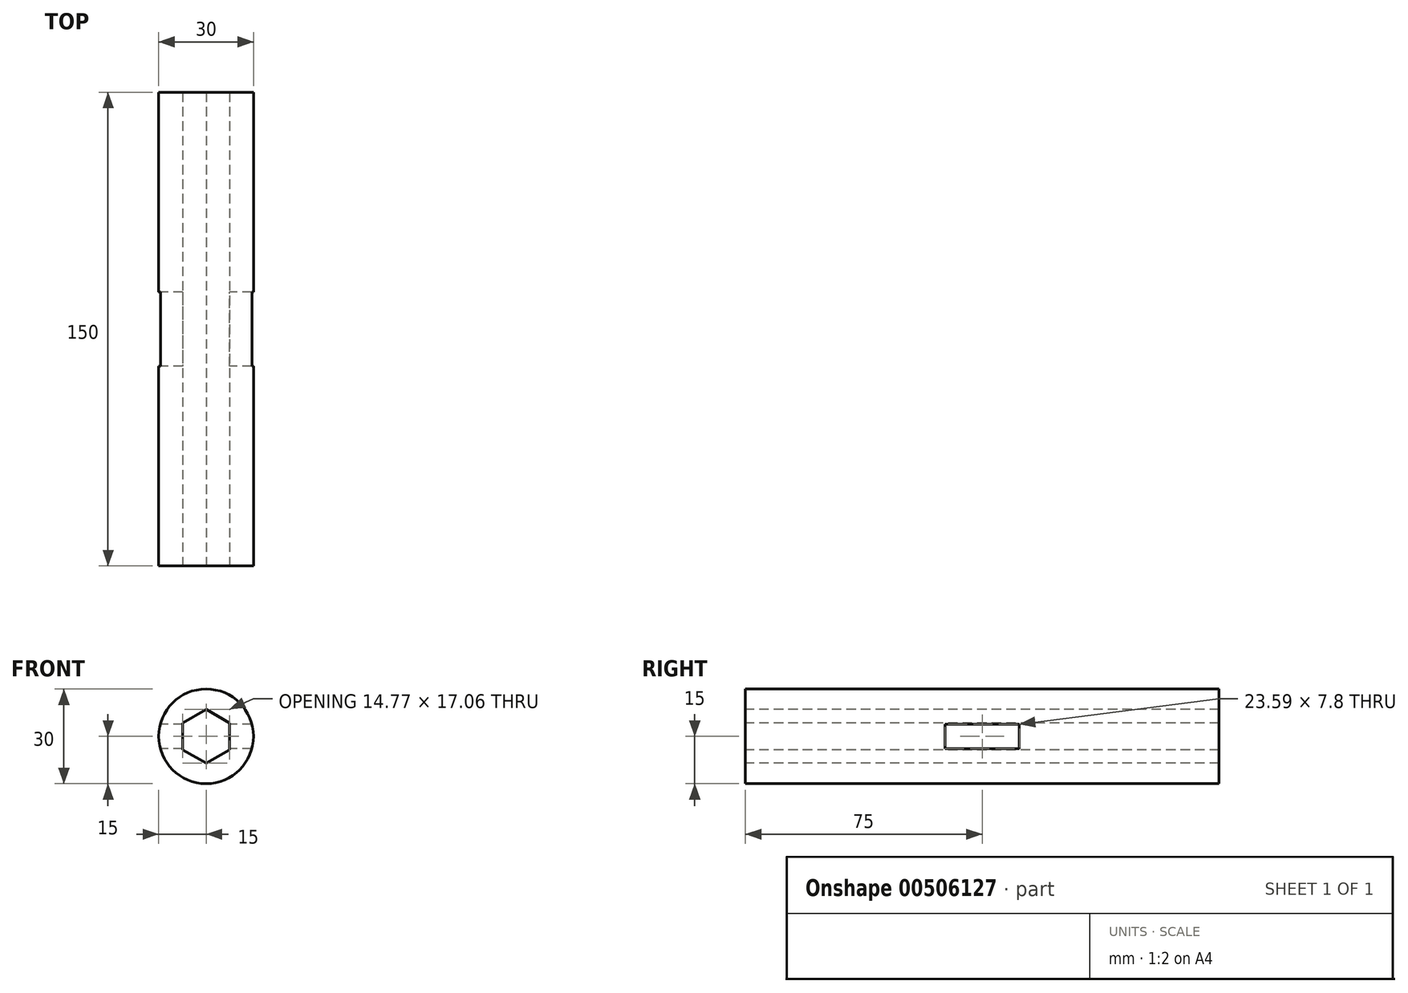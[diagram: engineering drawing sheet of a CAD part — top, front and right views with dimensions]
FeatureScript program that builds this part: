
annotation { "Feature Type Name" : "Feature", "Feature Type Description" : "" }
export const myFeature = defineFeature(function(context is Context, id is Id, definition is map)
    precondition{}
    {
        {
            var Q0;
            Q0=qCreatedBy(makeId("Front.planeOp"),FACE);
            var sketch = newSketch(context, id + "F0", { "sketchPlane" : qUnion([Q0])});
            skCircle(sketch, "E0", {"center": v(0, 0) * mm, "radius": 15 * mm});
            skSolve(sketch);
        }
        {
            var Q0;
            Q0=makeQuery(id+"F0.imprint","IMPRINT",FACE,{"disambiguationData":[TD([[makeQuery(id+"F0.imprint","IMPRINT",EDGE,{"derivedFrom":sQuery(id+"F0.wireOp",EDGE,"E0")}),1.0]])]});
            extrude(context, id + "F1", {"entities" : qUnion([Q0]), "endBound" : BoundingType.SYMMETRIC, "depth" : 150 * mm});
        }
        {
            var Q0;
            Q0=makeQuery(id+"F1.opExtrude","CAP_FACE",FACE,{"disambiguationData":[OSD([sQuery(id+"F0.wireOp",EDGE,"E0")])],"isStart":false});
            var sketch = newSketch(context, id + "F2", { "sketchPlane" : qUnion([Q0])});
            skCircle(sketch, "E1.cCircle", {"center": v(0, 0) * mm, "radius": 8.53 * mm, "construction": true});
            skLineSegment(sketch, "E1.0", {"start": v(0, -8.53) * mm, "end": v(-7.39, -4.26) * mm});
            skLineSegment(sketch, "E1.1", {"start": v(-7.39, -4.26) * mm, "end": v(-7.39, 4.26) * mm});
            skLineSegment(sketch, "E1.2", {"start": v(-7.39, 4.26) * mm, "end": v(0, 8.53) * mm});
            skLineSegment(sketch, "E1.3", {"start": v(0, 8.53) * mm, "end": v(7.39, 4.26) * mm});
            skLineSegment(sketch, "E1.4", {"start": v(7.39, 4.26) * mm, "end": v(7.39, -4.26) * mm});
            skLineSegment(sketch, "E1.5", {"start": v(7.39, -4.26) * mm, "end": v(0, -8.53) * mm});
            skSolve(sketch);
        }
        {
            var Q0;
            Q0=makeQuery(id+"F2.imprint","IMPRINT",FACE,{"disambiguationData":[TD([[makeQuery(id+"F2.imprint","IMPRINT",EDGE,{"derivedFrom":sQuery(id+"F2.wireOp",EDGE,"E1.0")}),-1.0]])]});
            extrude(context, id + "F3", {"entities" : qUnion([Q0]), "operationType" : NewBodyOperationType.REMOVE, "endBound" : BoundingType.SYMMETRIC, "oppositeDirection" : true, "depth" : 300 * mm});
        }
        {
            var Q0;
            Q0=qCreatedBy(makeId("Right.planeOp"),FACE);
            var sketch = newSketch(context, id + "F4", { "sketchPlane" : qUnion([Q0])});
            skLineSegment(sketch, "E2.bottom", {"start": v(-11.8, -3.9) * mm, "end": v(11.8, -3.9) * mm});
            skLineSegment(sketch, "E2.top", {"start": v(-11.8, 3.9) * mm, "end": v(11.8, 3.9) * mm});
            skLineSegment(sketch, "E2.left", {"start": v(-11.8, -3.9) * mm, "end": v(-11.8, 3.9) * mm});
            skLineSegment(sketch, "E2.right", {"start": v(11.8, -3.9) * mm, "end": v(11.8, 3.9) * mm});
            skPoint(sketch, "E2.middle", {"position": v(0, 0) * mm});
            skSolve(sketch);
        }
        {
            var Q0;
            Q0=makeQuery(id+"F4.imprint","IMPRINT",FACE,{"disambiguationData":[TD([[makeQuery(id+"F4.imprint","IMPRINT",EDGE,{"derivedFrom":sQuery(id+"F4.wireOp",EDGE,"E2.bottom")}),1.0]])]});
            extrude(context, id + "F5", {"entities" : qUnion([Q0]), "operationType" : NewBodyOperationType.REMOVE, "endBound" : BoundingType.SYMMETRIC, "depth" : 42 * mm});
        }
    });
